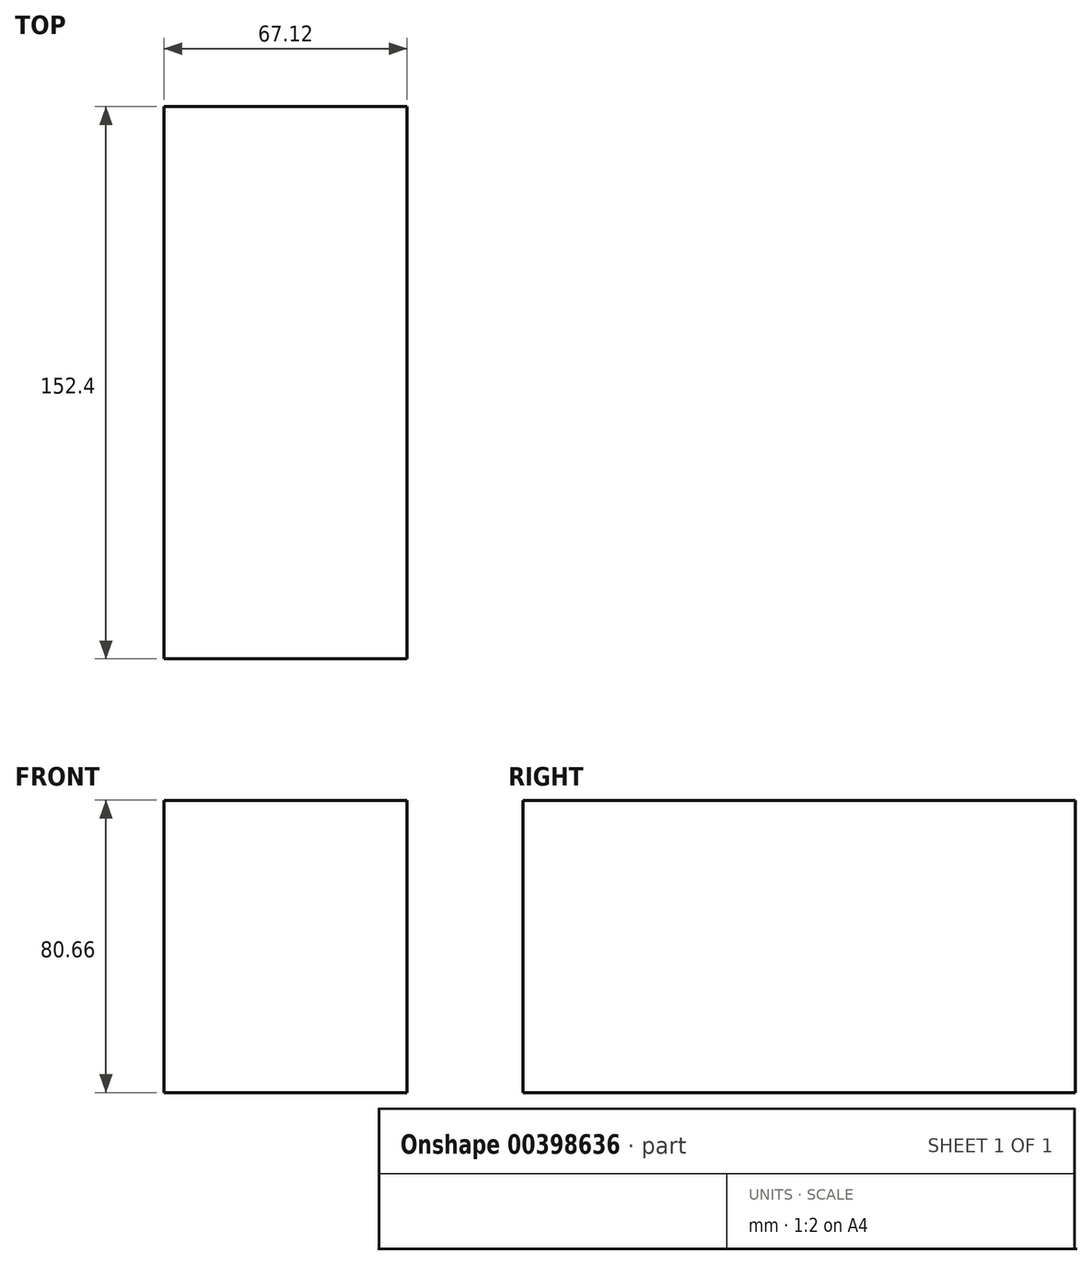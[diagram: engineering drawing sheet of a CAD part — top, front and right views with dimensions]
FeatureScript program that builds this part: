
annotation { "Feature Type Name" : "Feature", "Feature Type Description" : "" }
export const myFeature = defineFeature(function(context is Context, id is Id, definition is map)
    precondition{}
    {
        {
            var Q0;
            Q0=qCreatedBy(makeId("Front.planeOp"),FACE);
            var sketch = newSketch(context, id + "F0", { "sketchPlane" : qUnion([Q0])});
            skLineSegment(sketch, "E0.bottom", {"start": v(32.84, 35.55) * mm, "end": v(-34.28, 35.55) * mm});
            skLineSegment(sketch, "E0.top", {"start": v(32.84, -45.11) * mm, "end": v(-34.28, -45.11) * mm});
            skLineSegment(sketch, "E0.left", {"start": v(32.84, 35.55) * mm, "end": v(32.84, -45.11) * mm});
            skLineSegment(sketch, "E0.right", {"start": v(-34.28, 35.55) * mm, "end": v(-34.28, -45.11) * mm});
            skSolve(sketch);
        }
        {
            var Q0;
            Q0=makeQuery(id+"F0.imprint","IMPRINT",FACE,{"disambiguationData":[TD([[makeQuery(id+"F0.imprint","IMPRINT",EDGE,{"derivedFrom":sQuery(id+"F0.wireOp",EDGE,"E0.bottom")}),1.0]])]});
            extrude(context, id + "F1", {"entities" : qUnion([Q0]), "endBound" : BoundingType.SYMMETRIC, "depth" : 152.4 * mm});
        }
    });
